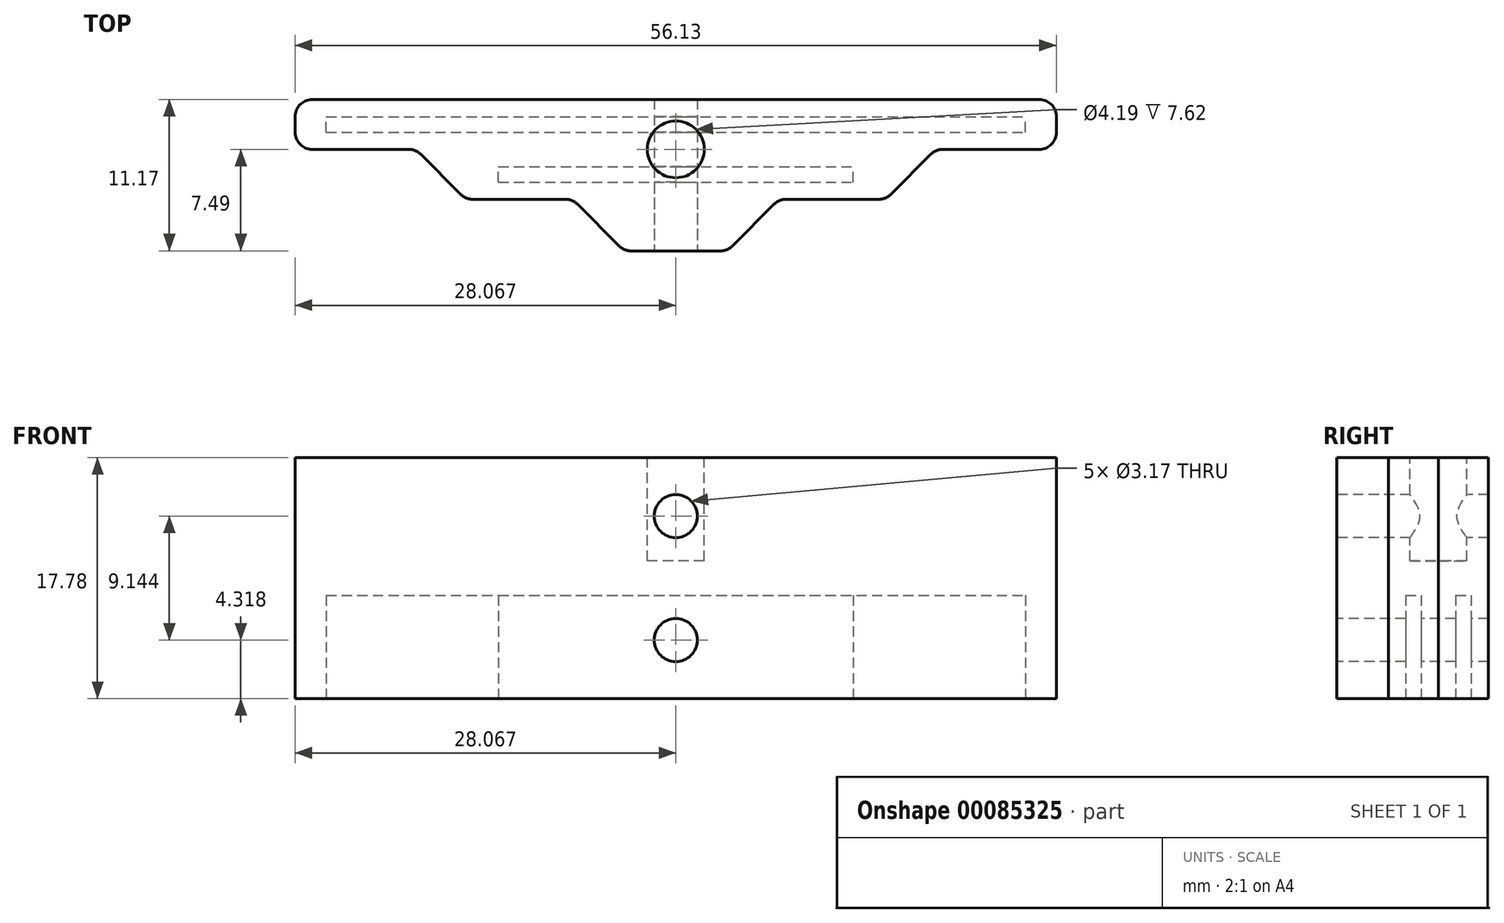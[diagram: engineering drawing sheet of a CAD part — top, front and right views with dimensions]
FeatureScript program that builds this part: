
annotation { "Feature Type Name" : "Feature", "Feature Type Description" : "" }
export const myFeature = defineFeature(function(context is Context, id is Id, definition is map)
    precondition{}
    {
        {
            var Q0;
            Q0=qCreatedBy(makeId("Top.planeOp"),FACE);
            var sketch = newSketch(context, id + "F0", { "sketchPlane" : qUnion([Q0])});
            skLineSegment(sketch, "E0.bottom", {"start": v(0, 0) * mm, "end": v(56.13, 0) * mm});
            skLineSegment(sketch, "E0.top", {"start": v(0, 3.68) * mm, "end": v(56.13, 3.68) * mm});
            skLineSegment(sketch, "E0.left", {"start": v(0, 0) * mm, "end": v(0, 3.68) * mm});
            skLineSegment(sketch, "E0.right", {"start": v(56.13, 0) * mm, "end": v(56.13, 3.68) * mm});
            skLineSegment(sketch, "E1", {"start": v(28.07, 3.68) * mm, "end": v(28.07, -22.08) * mm, "construction": true});
            skPoint(sketch, "E1.endSnap0", {"position": v(28.07, 0) * mm});
            skLineSegment(sketch, "E2.bottom", {"start": v(12.7, 0) * mm, "end": v(43.43, 0) * mm});
            skLineSegment(sketch, "E2.top", {"start": v(12.7, -3.68) * mm, "end": v(43.43, -3.68) * mm});
            skLineSegment(sketch, "E2.left", {"start": v(12.7, 0) * mm, "end": v(12.7, -3.68) * mm});
            skLineSegment(sketch, "E2.right", {"start": v(43.43, 0) * mm, "end": v(43.43, -3.68) * mm});
            skLineSegment(sketch, "E3.bottom", {"start": v(24.26, -3.68) * mm, "end": v(31.88, -3.68) * mm});
            skLineSegment(sketch, "E3.top", {"start": v(24.26, -7.5) * mm, "end": v(31.88, -7.5) * mm});
            skLineSegment(sketch, "E3.left", {"start": v(24.26, -3.68) * mm, "end": v(24.26, -7.5) * mm});
            skLineSegment(sketch, "E3.right", {"start": v(31.88, -3.68) * mm, "end": v(31.88, -7.5) * mm});
            skSolve(sketch);
        }
        {
            var Q0;
            Q0 = qSketchRegion(id + "F0", true);
            extrude(context, id + "F1", {"entities" : qUnion([Q0]), "depth" : 17.78 * mm});
        }
        {
            var Q0;
            Q0=makeQuery(id+"F1.opExtrude","CAP_FACE",FACE,{"disambiguationData":[OSD([sQuery(id+"F0.wireOp",EDGE,"E0.bottom"),sQuery(id+"F0.wireOp",EDGE,"E0.top"),sQuery(id+"F0.wireOp",EDGE,"E0.left"),sQuery(id+"F0.wireOp",EDGE,"E0.right"),sQuery(id+"F0.wireOp",EDGE,"E2.top"),sQuery(id+"F0.wireOp",EDGE,"E2.left"),sQuery(id+"F0.wireOp",EDGE,"E2.right"),sQuery(id+"F0.wireOp",EDGE,"E3.top"),sQuery(id+"F0.wireOp",EDGE,"E3.left"),sQuery(id+"F0.wireOp",EDGE,"E3.right")])],"isStart":true});
            var sketch = newSketch(context, id + "F2", { "sketchPlane" : qUnion([Q0])});
            skLineSegment(sketch, "E4", {"start": v(0, -1.84) * mm, "end": v(56.13, -1.84) * mm, "construction": true});
            skLineSegment(sketch, "E5", {"start": v(12.7, 1.84) * mm, "end": v(43.43, 1.84) * mm, "construction": true});
            skLineSegment(sketch, "E6", {"start": v(24.26, 5.59) * mm, "end": v(31.88, 5.59) * mm, "construction": true});
            skLineSegment(sketch, "E7", {"start": v(28.07, 7.5) * mm, "end": v(28.07, -3.68) * mm, "construction": true});
            skLineSegment(sketch, "E8.bottom", {"start": v(2.29, -1.27) * mm, "end": v(53.85, -1.27) * mm});
            skLineSegment(sketch, "E8.top", {"start": v(2.29, -2.41) * mm, "end": v(53.85, -2.41) * mm});
            skLineSegment(sketch, "E8.left", {"start": v(2.29, -1.27) * mm, "end": v(2.29, -2.41) * mm});
            skLineSegment(sketch, "E8.right", {"start": v(53.85, -1.27) * mm, "end": v(53.85, -2.41) * mm});
            skLineSegment(sketch, "E9.bottom", {"start": v(14.99, 2.41) * mm, "end": v(41.15, 2.41) * mm});
            skLineSegment(sketch, "E9.top", {"start": v(14.99, 1.27) * mm, "end": v(41.15, 1.27) * mm});
            skLineSegment(sketch, "E9.left", {"start": v(14.99, 2.41) * mm, "end": v(14.99, 1.27) * mm});
            skLineSegment(sketch, "E9.right", {"start": v(41.15, 2.41) * mm, "end": v(41.15, 1.27) * mm});
            skSolve(sketch);
        }
        {
            var Q0;
            Q0 = qSketchRegion(id + "F2", true);
            extrude(context, id + "F3", {"entities" : qUnion([Q0]), "operationType" : NewBodyOperationType.REMOVE, "oppositeDirection" : true, "depth" : 7.62 * mm});
        }
        {
            var Q0;
            Q0=makeQuery(id+"F1.opExtrude","SWEPT_EDGE",EDGE,{"disambiguationData":[OSD([sQuery(id+"F0.wireOp",EDGE,"E2.top"),sQuery(id+"F0.wireOp",EDGE,"E3.bottom"),sQuery(id+"F0.wireOp",EDGE,"E3.right")])]});
            var Q1;
            Q1=makeQuery(id+"F1.opExtrude","SWEPT_EDGE",EDGE,{"disambiguationData":[OSD([sQuery(id+"F0.wireOp",EDGE,"E0.bottom"),sQuery(id+"F0.wireOp",EDGE,"E2.bottom"),sQuery(id+"F0.wireOp",EDGE,"E2.right")])]});
            var Q2;
            Q2=makeQuery(id+"F1.opExtrude","SWEPT_EDGE",EDGE,{"disambiguationData":[OSD([sQuery(id+"F0.wireOp",EDGE,"E2.top"),sQuery(id+"F0.wireOp",EDGE,"E3.bottom"),sQuery(id+"F0.wireOp",EDGE,"E3.left")])]});
            var Q3;
            Q3=makeQuery(id+"F1.opExtrude","SWEPT_EDGE",EDGE,{"disambiguationData":[OSD([sQuery(id+"F0.wireOp",EDGE,"E0.bottom"),sQuery(id+"F0.wireOp",EDGE,"E2.bottom"),sQuery(id+"F0.wireOp",EDGE,"E2.left")])]});
            chamfer(context, id + "F4", {"entities" : qUnion([Q0, Q1, Q2, Q3]), "width" : 3.8 * mm, "tangentPropagation" : true});
        }
        {
            var Q0;
            Q0=makeQuery(id+"F1.opExtrude","SWEPT_FACE",FACE,{"disambiguationData":[OSD([sQuery(id+"F0.wireOp",EDGE,"E3.top")])]});
            var sketch = newSketch(context, id + "F5", { "sketchPlane" : qUnion([Q0])});
            skLineSegment(sketch, "E10", {"start": v(28.07, 17.78) * mm, "end": v(28.07, 0) * mm, "construction": true});
            skCircle(sketch, "E11", {"center": v(28.07, 13.46) * mm, "radius": 1.59 * mm});
            skCircle(sketch, "E12", {"center": v(28.07, 4.32) * mm, "radius": 1.59 * mm});
            skSolve(sketch);
        }
        {
            var Q0;
            Q0 = qSketchRegion(id + "F5", true);
            extrude(context, id + "F6", {"entities" : qUnion([Q0]), "operationType" : NewBodyOperationType.REMOVE, "oppositeDirection" : true, "depth" : 25.4 * mm});
        }
        {
            var Q0;
            Q0=makeQuery(id+"F1.opExtrude","CAP_FACE",FACE,{"disambiguationData":[OSD([sQuery(id+"F0.wireOp",EDGE,"E0.bottom"),sQuery(id+"F0.wireOp",EDGE,"E0.top"),sQuery(id+"F0.wireOp",EDGE,"E0.left"),sQuery(id+"F0.wireOp",EDGE,"E0.right"),sQuery(id+"F0.wireOp",EDGE,"E2.top"),sQuery(id+"F0.wireOp",EDGE,"E2.left"),sQuery(id+"F0.wireOp",EDGE,"E2.right"),sQuery(id+"F0.wireOp",EDGE,"E3.top"),sQuery(id+"F0.wireOp",EDGE,"E3.left"),sQuery(id+"F0.wireOp",EDGE,"E3.right")])],"isStart":false});
            var sketch = newSketch(context, id + "F7", { "sketchPlane" : qUnion([Q0])});
            skLineSegment(sketch, "E13", {"start": v(28.07, 3.68) * mm, "end": v(28.07, -7.5) * mm, "construction": true});
            skCircle(sketch, "E14", {"center": v(28.07, 0) * mm, "radius": 2.1 * mm});
            skSolve(sketch);
        }
        {
            var Q0;
            Q0=makeQuery(id+"F7.imprint","IMPRINT",FACE,{"disambiguationData":[TD([[makeQuery(id+"F7.imprint","IMPRINT",EDGE,{"derivedFrom":sQuery(id+"F7.wireOp",EDGE,"E14")}),1.0]])]});
            var Q1;
            Q1=sQuery(id+"F7.wireOp",EDGE,"E14");
            extrude(context, id + "F8", {"entities" : qUnion([Q0]), "operationType" : NewBodyOperationType.REMOVE, "surfaceEntities" : qUnion([Q1]), "oppositeDirection" : true, "depth" : 7.62 * mm});
        }
        {
            var Q0;
            Q0=makeQuery(id+"F1.opExtrude","SWEPT_EDGE",EDGE,{"disambiguationData":[OSD([sQuery(id+"F0.wireOp",EDGE,"E0.bottom"),sQuery(id+"F0.wireOp",EDGE,"E0.left")])]});
            var Q1;
            Q1=makeQuery(id+"F1.opExtrude","SWEPT_EDGE",EDGE,{"disambiguationData":[OSD([sQuery(id+"F0.wireOp",EDGE,"E0.bottom"),sQuery(id+"F0.wireOp",EDGE,"E0.right")])]});
            var Q2;
            Q2=makeQuery(id+"F1.opExtrude","SWEPT_EDGE",EDGE,{"disambiguationData":[OSD([sQuery(id+"F0.wireOp",EDGE,"E0.top"),sQuery(id+"F0.wireOp",EDGE,"E0.right")])]});
            var Q3;
            Q3=makeQuery(id+"F1.opExtrude","SWEPT_EDGE",EDGE,{"disambiguationData":[OSD([sQuery(id+"F0.wireOp",EDGE,"E0.top"),sQuery(id+"F0.wireOp",EDGE,"E0.left")])]});
            var Q4;
            {var subQ0=sQuery(id+"F0.wireOp",EDGE,"E2.left");var subQ1=sQuery(id+"F0.wireOp",EDGE,"E2.top");Q4=makeQuery(id+"F4.opChamfer","BLEND_EDGE",EDGE,{"blendedFrom":[makeQuery(id+"F1.opExtrude","SWEPT_EDGE",EDGE,{"disambiguationData":[OSD([sQuery(id+"F0.wireOp",EDGE,"E0.bottom"),sQuery(id+"F0.wireOp",EDGE,"E2.bottom"),subQ0])]}),makeQuery(id+"F1.opExtrude","SWEPT_FACE",FACE,{"disambiguationData":[OSD([subQ1]),TDD([makeQuery(id+"F0.imprint","IMPRINT",EDGE,{"disambiguationData":[TD([[makeQuery(id+"F0.imprint","INTERSECT",VERTEX,{"derivedFrom":[subQ1,subQ0]}),-1.0]])],"derivedFrom":subQ1})])]})],"blendedInto":[makeQuery(id+"F1.opExtrude","SWEPT_FACE",FACE,{"disambiguationData":[OSD([subQ1]),TDD([makeQuery(id+"F0.imprint","IMPRINT",EDGE,{"disambiguationData":[TD([[makeQuery(id+"F0.imprint","INTERSECT",VERTEX,{"derivedFrom":[subQ1,subQ0]}),-1.0]])],"derivedFrom":subQ1})])]})]});}
            var Q5;
            {var subQ0=sQuery(id+"F0.wireOp",EDGE,"E2.right");var subQ1=sQuery(id+"F0.wireOp",EDGE,"E2.top");Q5=makeQuery(id+"F4.opChamfer","BLEND_EDGE",EDGE,{"blendedFrom":[makeQuery(id+"F1.opExtrude","SWEPT_EDGE",EDGE,{"disambiguationData":[OSD([sQuery(id+"F0.wireOp",EDGE,"E0.bottom"),sQuery(id+"F0.wireOp",EDGE,"E2.bottom"),subQ0])]}),makeQuery(id+"F1.opExtrude","SWEPT_FACE",FACE,{"disambiguationData":[OSD([subQ1]),TDD([makeQuery(id+"F0.imprint","IMPRINT",EDGE,{"disambiguationData":[TD([[makeQuery(id+"F0.imprint","INTERSECT",VERTEX,{"derivedFrom":[subQ1,subQ0]}),1.0]])],"derivedFrom":subQ1})])]})],"blendedInto":[makeQuery(id+"F1.opExtrude","SWEPT_FACE",FACE,{"disambiguationData":[OSD([subQ1]),TDD([makeQuery(id+"F0.imprint","IMPRINT",EDGE,{"disambiguationData":[TD([[makeQuery(id+"F0.imprint","INTERSECT",VERTEX,{"derivedFrom":[subQ1,subQ0]}),1.0]])],"derivedFrom":subQ1})])]})]});}
            var Q6;
            Q6=makeQuery(id+"F4.opChamfer","BLEND_EDGE",EDGE,{"blendedFrom":[makeQuery(id+"F1.opExtrude","SWEPT_EDGE",EDGE,{"disambiguationData":[OSD([sQuery(id+"F0.wireOp",EDGE,"E2.top"),sQuery(id+"F0.wireOp",EDGE,"E3.bottom"),sQuery(id+"F0.wireOp",EDGE,"E3.right")])]}),makeQuery(id+"F1.opExtrude","SWEPT_FACE",FACE,{"disambiguationData":[OSD([sQuery(id+"F0.wireOp",EDGE,"E3.top")])]})],"blendedInto":[makeQuery(id+"F1.opExtrude","SWEPT_FACE",FACE,{"disambiguationData":[OSD([sQuery(id+"F0.wireOp",EDGE,"E3.top")])]})]});
            var Q7;
            Q7=makeQuery(id+"F4.opChamfer","BLEND_EDGE",EDGE,{"blendedFrom":[makeQuery(id+"F1.opExtrude","SWEPT_EDGE",EDGE,{"disambiguationData":[OSD([sQuery(id+"F0.wireOp",EDGE,"E2.top"),sQuery(id+"F0.wireOp",EDGE,"E3.bottom"),sQuery(id+"F0.wireOp",EDGE,"E3.left")])]}),makeQuery(id+"F1.opExtrude","SWEPT_FACE",FACE,{"disambiguationData":[OSD([sQuery(id+"F0.wireOp",EDGE,"E3.top")])]})],"blendedInto":[makeQuery(id+"F1.opExtrude","SWEPT_FACE",FACE,{"disambiguationData":[OSD([sQuery(id+"F0.wireOp",EDGE,"E3.top")])]})]});
            var Q8;
            {var subQ0=sQuery(id+"F0.wireOp",EDGE,"E0.bottom");var subQ1=sQuery(id+"F0.wireOp",EDGE,"E2.left");var subQ2=sQuery(id+"F0.wireOp",EDGE,"E2.bottom");Q8=makeQuery(id+"F4.opChamfer","BLEND_EDGE",EDGE,{"blendedFrom":[makeQuery(id+"F1.opExtrude","SWEPT_EDGE",EDGE,{"disambiguationData":[OSD([subQ0,subQ2,subQ1])]}),makeQuery(id+"F1.opExtrude","SWEPT_FACE",FACE,{"disambiguationData":[OSD([subQ0]),TDD([makeQuery(id+"F0.imprint","IMPRINT",EDGE,{"disambiguationData":[TD([[makeQuery(id+"F0.imprint","INTERSECT",VERTEX,{"derivedFrom":[subQ0,sQuery(id+"F0.wireOp",EDGE,"E0.left")]}),-1.0]])],"derivedFrom":subQ0})])]})],"blendedInto":[makeQuery(id+"F1.opExtrude","SWEPT_FACE",FACE,{"disambiguationData":[OSD([subQ0]),TDD([makeQuery(id+"F0.imprint","IMPRINT",EDGE,{"disambiguationData":[TD([[makeQuery(id+"F0.imprint","INTERSECT",VERTEX,{"derivedFrom":[subQ0,sQuery(id+"F0.wireOp",EDGE,"E0.left")]}),-1.0]])],"derivedFrom":subQ0})])]})]});}
            var Q9;
            {var subQ0=sQuery(id+"F0.wireOp",EDGE,"E0.bottom");var subQ1=sQuery(id+"F0.wireOp",EDGE,"E2.right");var subQ2=sQuery(id+"F0.wireOp",EDGE,"E2.bottom");Q9=makeQuery(id+"F4.opChamfer","BLEND_EDGE",EDGE,{"blendedFrom":[makeQuery(id+"F1.opExtrude","SWEPT_EDGE",EDGE,{"disambiguationData":[OSD([subQ0,subQ2,subQ1])]}),makeQuery(id+"F1.opExtrude","SWEPT_FACE",FACE,{"disambiguationData":[OSD([subQ0]),TDD([makeQuery(id+"F0.imprint","IMPRINT",EDGE,{"disambiguationData":[TD([[makeQuery(id+"F0.imprint","INTERSECT",VERTEX,{"derivedFrom":[subQ0,sQuery(id+"F0.wireOp",EDGE,"E0.right")]}),1.0]])],"derivedFrom":subQ0})])]})],"blendedInto":[makeQuery(id+"F1.opExtrude","SWEPT_FACE",FACE,{"disambiguationData":[OSD([subQ0]),TDD([makeQuery(id+"F0.imprint","IMPRINT",EDGE,{"disambiguationData":[TD([[makeQuery(id+"F0.imprint","INTERSECT",VERTEX,{"derivedFrom":[subQ0,sQuery(id+"F0.wireOp",EDGE,"E0.right")]}),1.0]])],"derivedFrom":subQ0})])]})]});}
            var Q10;
            {var subQ0=sQuery(id+"F0.wireOp",EDGE,"E2.top");var subQ1=sQuery(id+"F0.wireOp",EDGE,"E3.right");var subQ2=sQuery(id+"F0.wireOp",EDGE,"E3.bottom");Q10=makeQuery(id+"F4.opChamfer","BLEND_EDGE",EDGE,{"blendedFrom":[makeQuery(id+"F1.opExtrude","SWEPT_EDGE",EDGE,{"disambiguationData":[OSD([subQ0,subQ2,subQ1])]}),makeQuery(id+"F1.opExtrude","SWEPT_FACE",FACE,{"disambiguationData":[OSD([subQ0]),TDD([makeQuery(id+"F0.imprint","IMPRINT",EDGE,{"disambiguationData":[TD([[makeQuery(id+"F0.imprint","INTERSECT",VERTEX,{"derivedFrom":[subQ0,sQuery(id+"F0.wireOp",EDGE,"E2.right")]}),1.0]])],"derivedFrom":subQ0})])]})],"blendedInto":[makeQuery(id+"F1.opExtrude","SWEPT_FACE",FACE,{"disambiguationData":[OSD([subQ0]),TDD([makeQuery(id+"F0.imprint","IMPRINT",EDGE,{"disambiguationData":[TD([[makeQuery(id+"F0.imprint","INTERSECT",VERTEX,{"derivedFrom":[subQ0,sQuery(id+"F0.wireOp",EDGE,"E2.right")]}),1.0]])],"derivedFrom":subQ0})])]})]});}
            var Q11;
            {var subQ0=sQuery(id+"F0.wireOp",EDGE,"E2.top");var subQ1=sQuery(id+"F0.wireOp",EDGE,"E3.left");var subQ2=sQuery(id+"F0.wireOp",EDGE,"E3.bottom");Q11=makeQuery(id+"F4.opChamfer","BLEND_EDGE",EDGE,{"blendedFrom":[makeQuery(id+"F1.opExtrude","SWEPT_EDGE",EDGE,{"disambiguationData":[OSD([subQ0,subQ2,subQ1])]}),makeQuery(id+"F1.opExtrude","SWEPT_FACE",FACE,{"disambiguationData":[OSD([subQ0]),TDD([makeQuery(id+"F0.imprint","IMPRINT",EDGE,{"disambiguationData":[TD([[makeQuery(id+"F0.imprint","INTERSECT",VERTEX,{"derivedFrom":[subQ0,sQuery(id+"F0.wireOp",EDGE,"E2.left")]}),-1.0]])],"derivedFrom":subQ0})])]})],"blendedInto":[makeQuery(id+"F1.opExtrude","SWEPT_FACE",FACE,{"disambiguationData":[OSD([subQ0]),TDD([makeQuery(id+"F0.imprint","IMPRINT",EDGE,{"disambiguationData":[TD([[makeQuery(id+"F0.imprint","INTERSECT",VERTEX,{"derivedFrom":[subQ0,sQuery(id+"F0.wireOp",EDGE,"E2.left")]}),-1.0]])],"derivedFrom":subQ0})])]})]});}
            fillet(context, id + "F9", {"entities" : qUnion([Q0, Q1, Q2, Q3, Q4, Q5, Q6, Q7, Q8, Q9, Q10, Q11]), "radius" : 1.27 * mm, "tangentPropagation" : true, "allowEdgeOverflow" : false});
        }
    });
